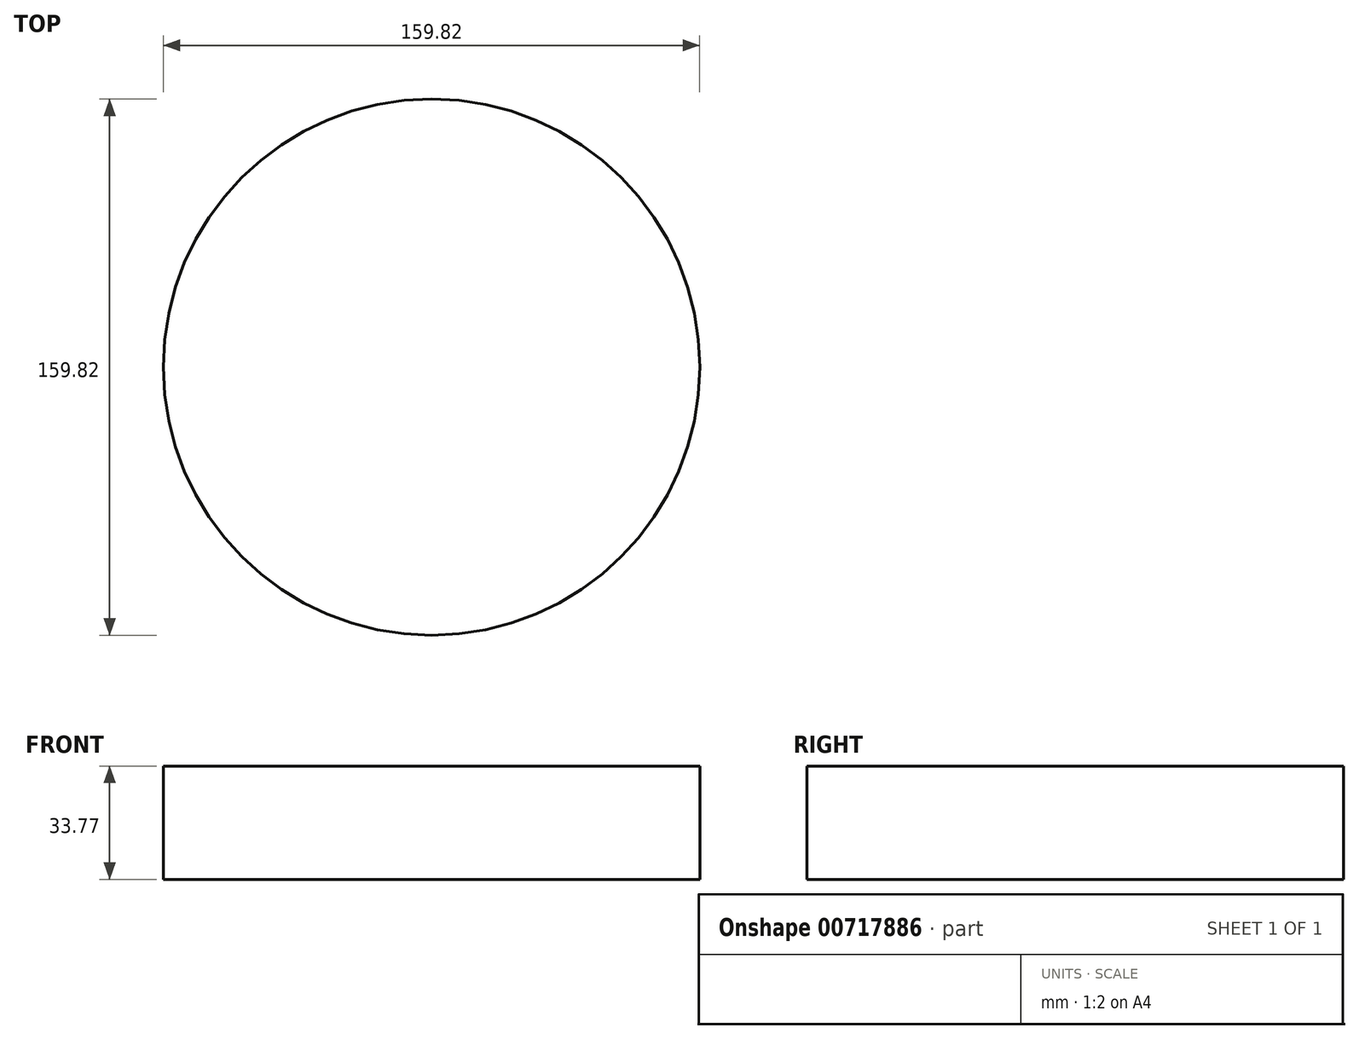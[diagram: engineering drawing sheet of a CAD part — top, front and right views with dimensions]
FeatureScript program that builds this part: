
annotation { "Feature Type Name" : "Feature", "Feature Type Description" : "" }
export const myFeature = defineFeature(function(context is Context, id is Id, definition is map)
    precondition{}
    {
        {
            var Q0;
            Q0=qCreatedBy(makeId("Front.planeOp"),FACE);
            var sketch = newSketch(context, id + "F0", { "sketchPlane" : qUnion([Q0])});
            skLineSegment(sketch, "E0.bottom", {"start": v(0, 0) * mm, "end": v(79.91, 0) * mm});
            skLineSegment(sketch, "E0.top", {"start": v(0, 33.77) * mm, "end": v(79.91, 33.77) * mm});
            skLineSegment(sketch, "E0.left", {"start": v(0, 0) * mm, "end": v(0, 33.77) * mm});
            skLineSegment(sketch, "E0.right", {"start": v(79.91, 0) * mm, "end": v(79.91, 33.77) * mm});
            skSolve(sketch);
        }
        {
            var Q0;
            Q0=makeQuery(id+"F0.imprint","IMPRINT",FACE,{"disambiguationData":[TD([[makeQuery(id+"F0.imprint","IMPRINT",EDGE,{"derivedFrom":sQuery(id+"F0.wireOp",EDGE,"E0.bottom")}),1.0]])]});
            var Q1;
            Q1=sQuery(id+"F0.wireOp",EDGE,"E0.left");
            revolve(context, id + "F1", {"surfaceOperationType" : NewSurfaceOperationType.NEW, "entities" : qUnion([Q0]), "axis" : qUnion([Q1]), "revolveType" : RevolveType.FULL});
        }
    });
